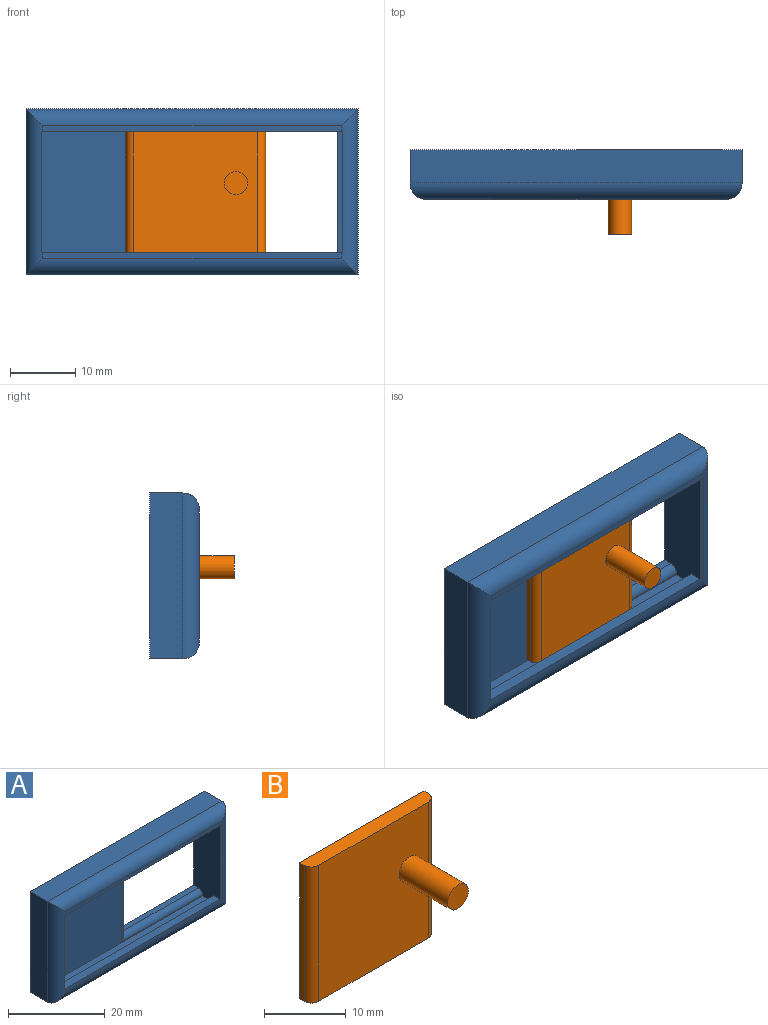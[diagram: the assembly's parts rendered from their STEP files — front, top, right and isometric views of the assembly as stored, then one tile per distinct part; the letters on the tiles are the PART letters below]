
ASSEMBLY  parts=2 mates=1
PART A: 28 faces, bbox 50.8x7.6x25.4 mm
  f0: plane 45.27x3.18mm, normal (0,0,1), area 144.1mm2, adj f2,f6,f12,f19
  f1: plane 45.27x3.18mm, normal (0,0,-1), area 144.1mm2, adj f2,f3,f12,f19
  f2: plane 45.27x21.97mm, normal (0,-1,0), area 489.3mm2, adj f0,f1,f12,f19,f25,f26,f27
  f3: plane 45.27x1.71mm, normal (0,1,0), area 77.6mm2, adj f1,f4,f12,f19
  f4: plane 46.15x1.91mm, normal (0,0,-1), area 86.2mm2, adj f3,f12,f16,f18,f19,f20,f21,f23
  f5: plane 46.15x1.91mm, normal (0,0,1), area 86.2mm2, adj f6,f12,f17,f18,f19,f20,f21,f23
  f6: plane 45.27x1.71mm, normal (0,1,0), area 77.6mm2, adj f0,f5,f12,f19
  f7: plane 25.4x5.08mm, normal (-1,0,0), area 129mm2, adj f8,f9,f15,f23
  f8: plane 50.8x5.08mm, normal (0,0,1), area 258.1mm2, adj f7,f14,f15,f24
  f9: plane 50.8x5.08mm, normal (0,0,-1), area 258.1mm2, adj f7,f14,f15,f22
  f10: plane 18.91x1.26mm, normal (1,0,0), area 23.8mm2, adj f11,f13,f15,f27
  f11: plane 22.29x1.26mm, normal (0,0,-1), area 28.1mm2, adj f10,f12,f15,f26
  f12: plane 21.97x7.61mm, normal (-1,0,0), area 153.7mm2, adj f0,f1,f2,f3,f4,f5,f6,f11
  f13: plane 22.29x1.26mm, normal (0,0,1), area 28.1mm2, adj f10,f12,f15,f25
  f14: plane 25.4x5.08mm, normal (1,0,0), area 129mm2, adj f8,f9,f15,f21
  f15: plane 50.8x25.4mm, normal (0,1,0), area 868.9mm2, adj f7,f8,f9,f10,f11,f12,f13,f14
  f16: plane 45.72x0.89mm, normal (0,-1,0), area 40.6mm2, adj f4,f21,f23,f24
  f17: plane 45.72x0.89mm, normal (0,-1,0), area 40.6mm2, adj f5,f21,f22,f23
  f18: plane 18.54x0.79mm, normal (0,-1,0), area 14.6mm2, adj f4,f5,f12,f21
  f19: plane 21.97x5.08mm, normal (1,0,0), area 105.1mm2, adj f0,f1,f2,f3,f4,f5,f6,f20
  f20: plane 18.54x0.1mm, normal (0,-1,0), area 1.8mm2, adj f4,f5,f19,f23
  f21: cylinder r=2.54mm len=25.4mm, axis (0,0,1), area 89.9mm2, adj f4,f5,f14,f16,f17,f18,f22,f24
  f22: cylinder r=2.54mm len=50.8mm, axis (-1,0,0), area 195.3mm2, adj f9,f17,f21,f23
  f23: cylinder r=2.54mm len=25.4mm, axis (0,0,-1), area 89.9mm2, adj f4,f5,f7,f16,f17,f20,f22,f24
  f24: cylinder r=2.54mm len=50.8mm, axis (1,0,0), area 195.3mm2, adj f8,f16,f21,f23
  f25: cylinder r=1.27mm len=23.56mm, axis (1,0,0), area 45.4mm2, adj f2,f12,f13,f27
  f26: cylinder r=1.27mm len=23.56mm, axis (-1,0,0), area 45.4mm2, adj f2,f11,f12,f27
  f27: cylinder r=1.27mm len=21.45mm, axis (0,0,-1), area 39.6mm2, adj f2,f10,f25,f26
PART B: 10 faces, bbox 21.4x10.4x20.3 mm
  f0: plane 21.44x2.03mm, normal (0,0,-1), area 42.9mm2, adj f1,f3,f4,f5,f6,f7
  f1: plane 20.3x18.9mm, normal (0,-1,0), area 373.7mm2, adj f0,f2,f6,f7,f8
  f2: plane 21.44x2.03mm, normal (0,0,1), area 42.9mm2, adj f1,f3,f4,f5,f6,f7
  f3: plane 21.44x20.3mm, normal (0,1,0), area 435.3mm2, adj f0,f2,f4,f5
  f4: plane 20.3x0.76mm, normal (1,0,0), area 15.5mm2, adj f0,f2,f3,f7
  f5: plane 20.3x0.76mm, normal (-1,0,0), area 15.5mm2, adj f0,f2,f3,f6
  f6: cylinder r=1.27mm len=20.3mm, axis (0,0,1), area 40.5mm2, adj f0,f1,f2,f5
  f7: cylinder r=1.27mm len=20.3mm, axis (0,0,-1), area 40.5mm2, adj f0,f1,f2,f4
  f8: cylinder r=1.78mm len=8.38mm, axis (0,1,0), area 93.8mm2, adj f1,f9
  f9: plane 3.56x3.56mm, normal (0,-1,0), area 10mm2, adj f8
PLACE A t=(1.2,15.3,2.32)mm
PLACE B t=(13.7,15.87,1.83)mm
MATE planar B.f3 <-> A.f2  axis (0,1,0) through (-1.85,12.77,5.98)mm
